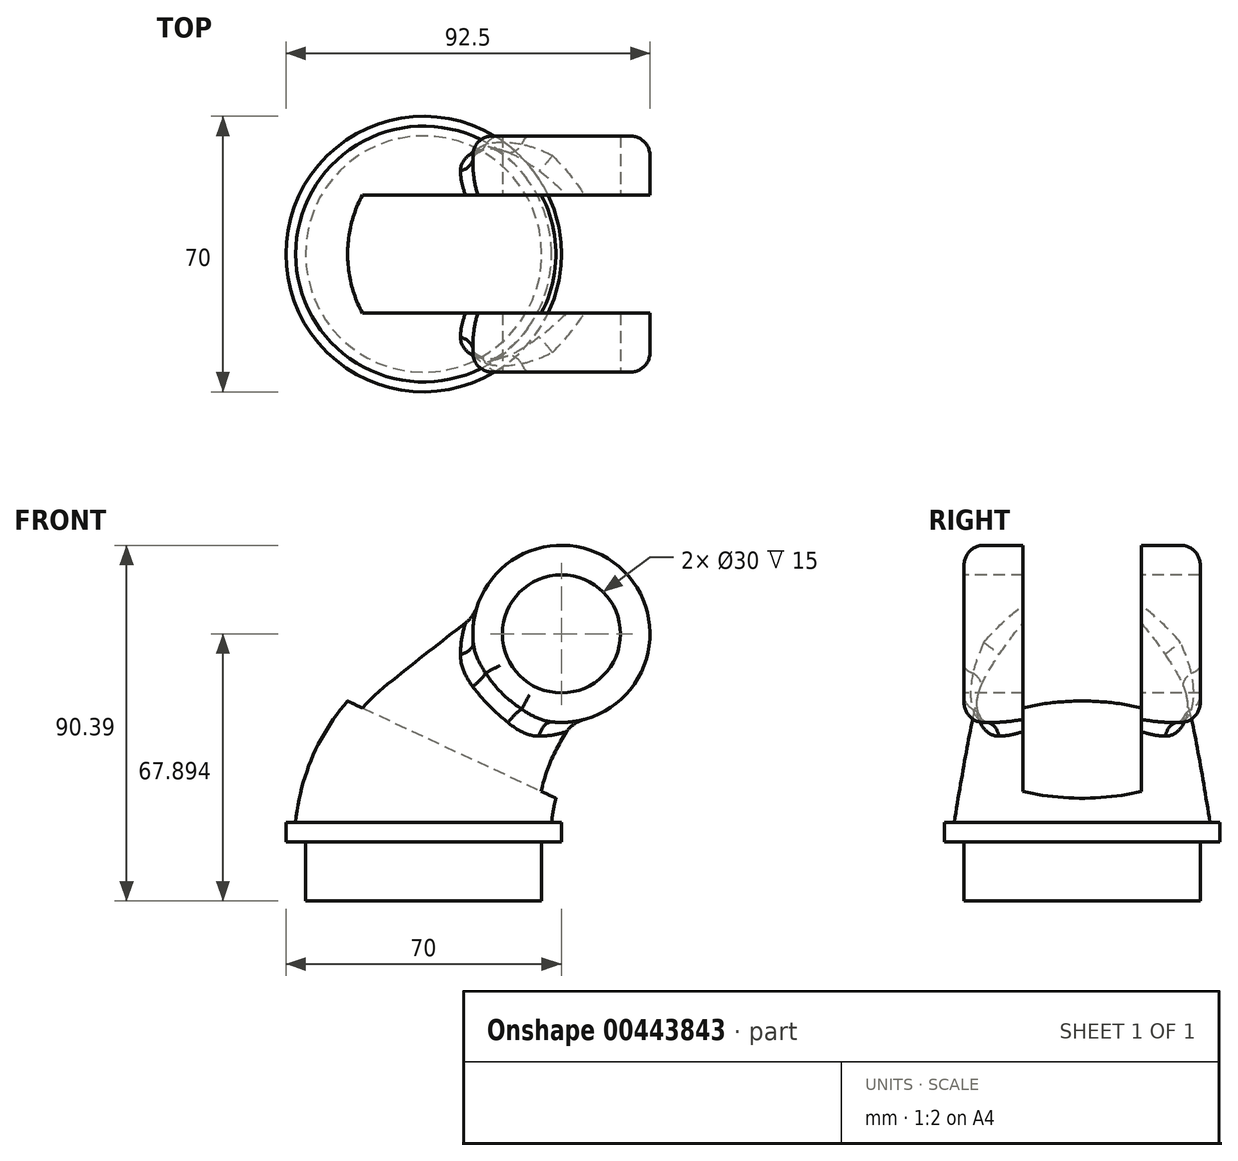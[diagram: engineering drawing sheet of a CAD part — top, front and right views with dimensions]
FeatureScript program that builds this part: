
annotation { "Feature Type Name" : "Feature", "Feature Type Description" : "" }
export const myFeature = defineFeature(function(context is Context, id is Id, definition is map)
    precondition{}
    {
        {
            var Q0;
            Q0=qCreatedBy(makeId("Top.planeOp"),FACE);
            var sketch = newSketch(context, id + "F0", { "sketchPlane" : qUnion([Q0])});
            skCircle(sketch, "E0", {"center": v(0, 0) * mm, "radius": 35 * mm});
            skSolve(sketch);
        }
        {
            var Q0;
            Q0 = qSketchRegion(id + "F0", true);
            extrude(context, id + "F1", {"entities" : qUnion([Q0]), "depth" : 5 * mm});
        }
        {
            var Q0;
            Q0=qCreatedBy(makeId("Front.planeOp"),FACE);
            var sketch = newSketch(context, id + "F2", { "sketchPlane" : qUnion([Q0])});
            skArc(sketch, "E1", {"start": v(17.6, 38.3) * mm, "mid": v(5.55, 23.37) * mm, "end": v(0, 5) * mm});
            skLineSegment(sketch, "E2", {"start": v(35, 52.9) * mm, "end": v(17.6, 38.3) * mm});
            skSolve(sketch);
        }
        {
            var Q0;
            Q0=sQuery(id+"F2.wireOp",EDGE,"E2");
            var Q1;
            Q1=sQuery(id+"F2.wireOp",VERTEX,"E2.start");
            cPlane(context, id + "F3", {"entities" : qUnion([Q0, Q1]), "cplaneType" : CPlaneType.LINE_POINT, "offset" : 25 * mm, "width" : 150 * mm, "height" : 150 * mm});
        }
        {
            var Q0;
            Q0=qCreatedBy(id+"F3.planeOp",FACE);
            var sketch = newSketch(context, id + "F4", { "sketchPlane" : qUnion([Q0])});
            skCircle(sketch, "E3", {"center": v(0, 18.02) * mm, "radius": 22.5 * mm});
            skSolve(sketch);
        }
        {
            var Q0;
            Q0=makeQuery(id+"F1.opExtrude","CAP_FACE",FACE,{"disambiguationData":[OSD([sQuery(id+"F0.wireOp",EDGE,"E0")])],"isStart":false});
            var sketch = newSketch(context, id + "F5", { "sketchPlane" : qUnion([Q0])});
            skCircle(sketch, "E4", {"center": v(0, 0) * mm, "radius": 32.5 * mm});
            skSolve(sketch);
        }
        {
            var Q0;
            Q0=qCreatedBy(makeId("Front.planeOp"),FACE);
            var sketch = newSketch(context, id + "F6", { "sketchPlane" : qUnion([Q0])});
            skArc(sketch, "E5", {"start": v(-13.25, 41.78) * mm, "mid": v(-26.5, 25.3) * mm, "end": v(-32.5, 5) * mm});
            skLineSegment(sketch, "E6", {"start": v(-13.25, 41.78) * mm, "end": v(20.54, 70.13) * mm});
            skSolve(sketch);
        }
        {
            var Q0;
            Q0=qCreatedBy(makeId("Front.planeOp"),FACE);
            var sketch = newSketch(context, id + "F7", { "sketchPlane" : qUnion([Q0])});
            skArc(sketch, "E7", {"start": v(48.46, 34.82) * mm, "mid": v(37.6, 21.45) * mm, "end": v(32.5, 5) * mm});
            skLineSegment(sketch, "E8", {"start": v(48.46, 34.82) * mm, "end": v(49.46, 35.66) * mm});
            skSolve(sketch);
        }
        {
            var Q1;
            Q1=makeQuery(id+"F5.imprint","IMPRINT",FACE,{"disambiguationData":[TD([[makeQuery(id+"F5.imprint","IMPRINT",EDGE,{"derivedFrom":sQuery(id+"F5.wireOp",EDGE,"E4")}),1.0]])]});
            var Q2;
            Q2=makeQuery(id+"F4.imprint","IMPRINT",FACE,{"disambiguationData":[TD([[makeQuery(id+"F4.imprint","IMPRINT",EDGE,{"derivedFrom":sQuery(id+"F4.wireOp",EDGE,"E3")}),1.0]])]});
            var Q3;
            Q3 = qConstructionFilter(qBodyType(qCreatedBy(id + "F6" ,EDGE), BodyType.WIRE), ConstructionObject.NO);
            var Q4;
            Q4 = qConstructionFilter(qBodyType(qCreatedBy(id + "F7" ,EDGE), BodyType.WIRE), ConstructionObject.NO);
            loft(context, id + "F8", {"operationType" : NewBodyOperationType.ADD, "addGuides" : true, "sheetProfilesArray" : [{ "sheetProfileEntities" : qUnion([Q1]) }, { "sheetProfileEntities" : qUnion([Q2]) }], "guidesArray" : [{ "guideEntities" : qUnion([Q3]), "guideDerivativeType" : LoftGuideDerivativeType.DEFAULT, "guideDerivativeMagnitude" : 1 }, { "guideEntities" : qUnion([Q4]), "guideDerivativeType" : LoftGuideDerivativeType.DEFAULT, "guideDerivativeMagnitude" : 1 }]});
        }
        {
            var Q0;
            Q0=qCreatedBy(makeId("Front.planeOp"),FACE);
            var sketch = newSketch(context, id + "F9", { "sketchPlane" : qUnion([Q0])});
            skCircle(sketch, "E9", {"center": v(35, 52.9) * mm, "radius": 22.5 * mm});
            skSolve(sketch);
        }
        {
            var Q0;
            Q0 = qSketchRegion(id + "F9", true);
            extrude(context, id + "F10", {"entities" : qUnion([Q0]), "operationType" : NewBodyOperationType.ADD, "endBound" : BoundingType.SYMMETRIC, "depth" : 60 * mm});
        }
        {
            var Q0;
            Q0=makeQuery(id+"F10.opExtrude","CAP_EDGE",EDGE,{"disambiguationData":[OSD([sQuery(id+"F9.wireOp",EDGE,"E9")])],"isStart":true});
            var Q1;
            Q1=makeQuery(id+"F10.opExtrude","CAP_EDGE",EDGE,{"disambiguationData":[OSD([sQuery(id+"F9.wireOp",EDGE,"E9")])],"isStart":false});
            fillet(context, id + "F11", {"entities" : qUnion([Q0, Q1]), "radius" : 5 * mm, "tangentPropagation" : true, "allowEdgeOverflow" : false});
        }
        {
            var Q0;
            Q0=makeQuery(id+"F10.boolean.opBoolean","INTERSECT",EDGE,{"disambiguationData":[OD(1.0)],"derivedFrom":[makeQuery(id+"F8.opLoft","SWEPT_FACE",FACE,{"disambiguationData":[OSD([sQuery(id+"F4.wireOp",EDGE,"E3"),sQuery(id+"F5.wireOp",EDGE,"E4"),sQuery(id+"F6.wireOp",VERTEX,"E6.start"),sQuery(id+"F6.wireOp",EDGE,"E5"),sQuery(id+"F6.wireOp",EDGE,"E6"),sQuery(id+"F7.wireOp",VERTEX,"E8.start"),sQuery(id+"F7.wireOp",EDGE,"E7"),sQuery(id+"F7.wireOp",EDGE,"E8")])]}),makeQuery(id+"F10.opExtrude","SWEPT_FACE",FACE,{"disambiguationData":[OSD([sQuery(id+"F9.wireOp",EDGE,"E9")])]})]});
            var Q1;
            Q1=makeQuery(id+"F10.boolean.opBoolean","INTERSECT",EDGE,{"disambiguationData":[OD(0.0)],"derivedFrom":[makeQuery(id+"F8.opLoft","SWEPT_FACE",FACE,{"disambiguationData":[OSD([sQuery(id+"F4.wireOp",EDGE,"E3"),sQuery(id+"F5.wireOp",EDGE,"E4"),sQuery(id+"F6.wireOp",VERTEX,"E6.start"),sQuery(id+"F6.wireOp",EDGE,"E5"),sQuery(id+"F6.wireOp",EDGE,"E6"),sQuery(id+"F7.wireOp",VERTEX,"E8.start"),sQuery(id+"F7.wireOp",EDGE,"E7"),sQuery(id+"F7.wireOp",EDGE,"E8")])]}),makeQuery(id+"F10.opExtrude","SWEPT_FACE",FACE,{"disambiguationData":[OSD([sQuery(id+"F9.wireOp",EDGE,"E9")])]})]});
            fillet(context, id + "F12", {"entities" : qUnion([Q0, Q1]), "radius" : 5 * mm, "tangentPropagation" : true, "allowEdgeOverflow" : false});
        }
        {
            var Q0;
            Q0=makeQuery(id+"F10.opExtrude","CAP_FACE",FACE,{"disambiguationData":[OSD([sQuery(id+"F9.wireOp",EDGE,"E9")])],"isStart":false});
            var sketch = newSketch(context, id + "F13", { "sketchPlane" : qUnion([Q0])});
            skCircle(sketch, "E10", {"center": v(35, 52.9) * mm, "radius": 15 * mm});
            skSolve(sketch);
        }
        {
            var Q0;
            Q0 = qSketchRegion(id + "F13", true);
            extrude(context, id + "F14", {"entities" : qUnion([Q0]), "operationType" : NewBodyOperationType.REMOVE, "endBound" : BoundingType.THROUGH_ALL, "oppositeDirection" : true, "depth" : 25 * mm});
        }
        {
            var Q0;
            Q0=qCreatedBy(makeId("Front.planeOp"),FACE);
            var sketch = newSketch(context, id + "F15", { "sketchPlane" : qUnion([Q0])});
            skLineSegment(sketch, "E11", {"start": v(-104.18, 75.4) * mm, "end": v(57.5, 0) * mm});
            skLineSegment(sketch, "E12", {"start": v(57.5, 75.4) * mm, "end": v(57.5, 0) * mm});
            skLineSegment(sketch, "E13", {"start": v(-104.18, 75.4) * mm, "end": v(57.5, 75.4) * mm});
            skSolve(sketch);
        }
        {
            var Q0;
            Q0 = qSketchRegion(id + "F15", true);
            extrude(context, id + "F16", {"entities" : qUnion([Q0]), "operationType" : NewBodyOperationType.REMOVE, "endBound" : BoundingType.SYMMETRIC, "depth" : 30 * mm});
        }
        {
            var Q0;
            Q0=qCreatedBy(makeId("Front.planeOp"),FACE);
            var sketch = newSketch(context, id + "F17", { "sketchPlane" : qUnion([Q0])});
            skLineSegment(sketch, "E14.bottom", {"start": v(0, 0) * mm, "end": v(-30, 0) * mm});
            skLineSegment(sketch, "E14.top", {"start": v(0, -15) * mm, "end": v(-30, -15) * mm});
            skLineSegment(sketch, "E14.left", {"start": v(0, 0) * mm, "end": v(0, -15) * mm});
            skLineSegment(sketch, "E14.right", {"start": v(-30, 0) * mm, "end": v(-30, -15) * mm});
            skSolve(sketch);
        }
        {
            var Q0;
            Q0 = qSketchRegion(id + "F17", true);
            var Q1;
            Q1=sQuery(id+"F17.wireOp",EDGE,"E14.left");
            revolve(context, id + "F18", {"operationType" : NewBodyOperationType.ADD, "entities" : qUnion([Q0]), "axis" : qUnion([Q1]), "revolveType" : RevolveType.FULL});
        }
    });
